# Revit family: DST_A3-Natural-Creation-Single-Side-Hung-32
name_source: partatom
category: Doors
revit_build: Autodesk Revit 2016 (Build: 20150220_1215(x64)
units: mm (PartAtom-declared; Revit-internal decimal feet)

## family parameters
Always vertical = Yes
Cut with Voids When Loaded = No
Host = Wall
Room Calculation Point = No
Shared = No

## types (2) — shared parameters
Assembly Code = B2030120
Construction Type = Steel
Function = Interior
Height = 2100 mm  [stored 6.88976 ft]
Manufacturer = Durowin
Material Door Frame = Default Steel Door Frame
Material Door Panel = Default Steel Door Panel
Material Glass = Glass
Model = Natural Creations
Model Type = Side Hung
Rough Height = 2122 mm  [stored 6.96194 ft]
Rough Width = 964 mm  [stored 3.16273 ft]
URL = www.Durowin.com
Wall Closure = By host
zero-valued in all types: Thickness

## per-type parameters (varying)
| type | Manufacturer Code | Panel Width | Width |
| 820 x 2100 C32 Natural Creation Single Side Hung | C32 | 800 mm  [stored 2.62467 ft] | 820 mm  [stored 2.69029 ft] |
| 920 x 2100 D32 | D32 | 900 mm | 920 mm  [stored 3.01837 ft] |

note: [stored X ft] marks values corroborated as IEEE doubles in the binary element streams (Revit-internal decimal feet)

## geometry (parser evidence)
native form markers: Sweep x4
no freeform markers — native parametric forms only
